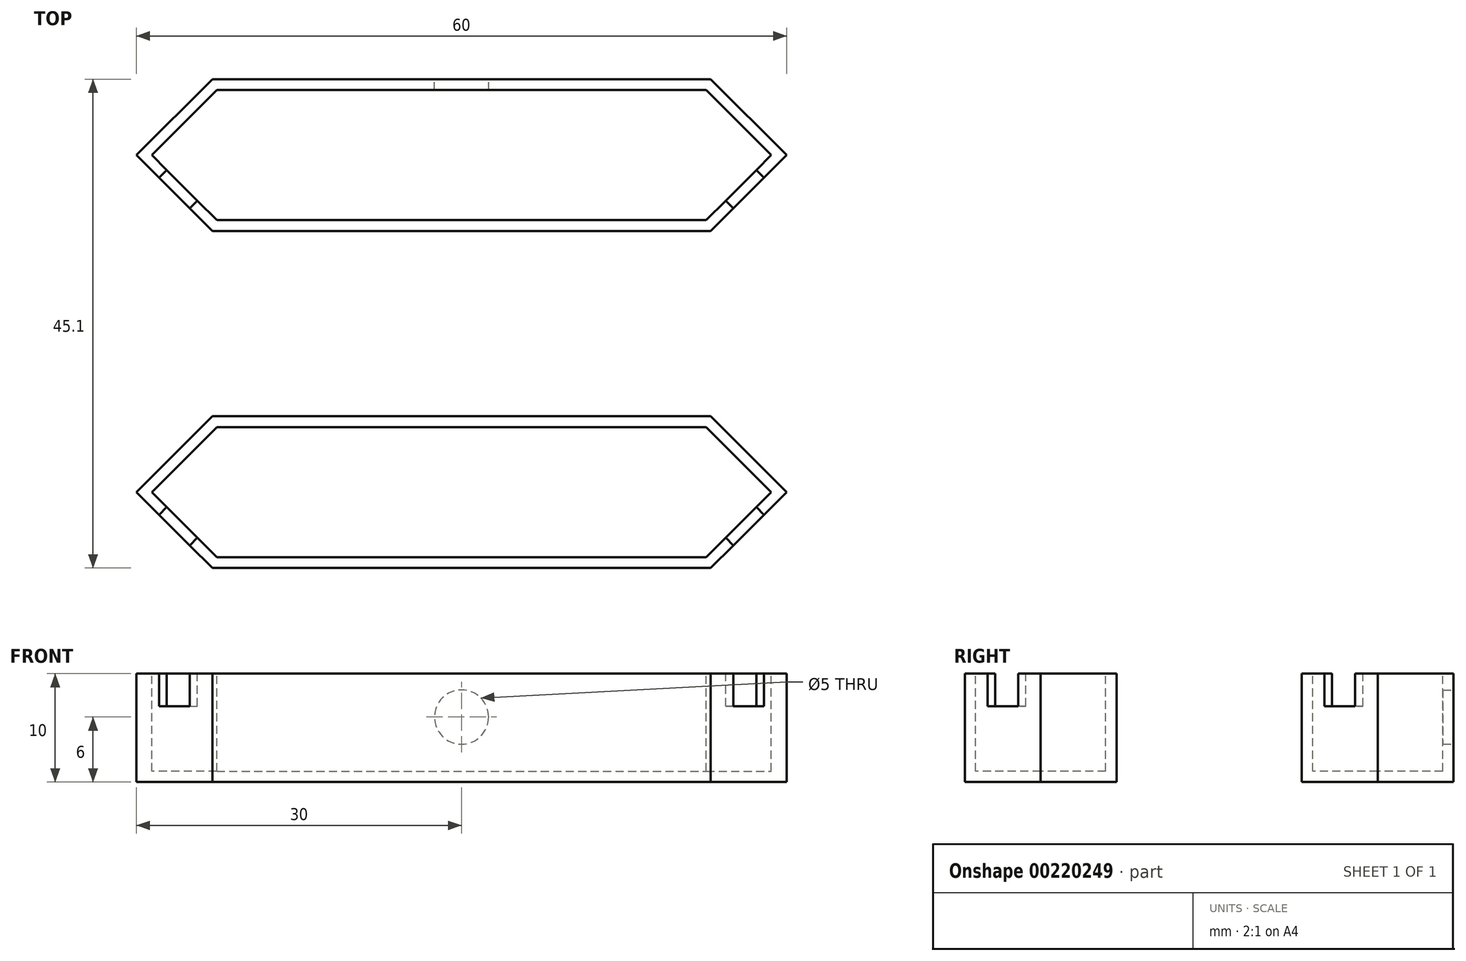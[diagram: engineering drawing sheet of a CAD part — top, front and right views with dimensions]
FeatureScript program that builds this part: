
annotation { "Feature Type Name" : "Feature", "Feature Type Description" : "" }
export const myFeature = defineFeature(function(context is Context, id is Id, definition is map)
    precondition{}
    {
        {
            assignVariable(context, id + "F0", {"name" : "breite", "anyValue" : 14});
        }
        {
            assignVariable(context, id + "F1", {"name" : "hoehe", "anyValue" : 10});
        }
        {
            assignVariable(context, id + "F2", {"name" : "wandung", "anyValue" : 1});
        }
        {
            var Q0;
            Q0=qCreatedBy(makeId("Top.planeOp"),FACE);
            var sketch = newSketch(context, id + "F3", { "sketchPlane" : qUnion([Q0])});
            skLineSegment(sketch, "E0.bottom", {"start": v(-30, 7) * mm, "end": v(30, 7) * mm});
            skLineSegment(sketch, "E0.top", {"start": v(-30, -7) * mm, "end": v(30, -7) * mm});
            skLineSegment(sketch, "E0.left", {"start": v(-30, 7) * mm, "end": v(-30, -7) * mm});
            skLineSegment(sketch, "E0.right", {"start": v(30, 7) * mm, "end": v(30, -7) * mm});
            skSolve(sketch);
        }
        {
            var Q0;
            Q0=makeQuery(id+"F3.imprint","IMPRINT",FACE,{"disambiguationData":[TD([[makeQuery(id+"F3.imprint","IMPRINT",EDGE,{"derivedFrom":sQuery(id+"F3.wireOp",EDGE,"E0.bottom")}),-1.0]])]});
            extrude(context, id + "F4", {"entities" : qUnion([Q0]), "depth" : (getVariable(context, 'hoehe')) * mm});
        }
        {
            var Q0;
            Q0=makeQuery(id+"F4.opExtrude","SWEPT_EDGE",EDGE,{"disambiguationData":[OSD([sQuery(id+"F3.wireOp",EDGE,"E0.top"),sQuery(id+"F3.wireOp",EDGE,"E0.left")])]});
            var Q1;
            Q1=makeQuery(id+"F4.opExtrude","SWEPT_EDGE",EDGE,{"disambiguationData":[OSD([sQuery(id+"F3.wireOp",EDGE,"E0.bottom"),sQuery(id+"F3.wireOp",EDGE,"E0.left")])]});
            var Q2;
            Q2=makeQuery(id+"F4.opExtrude","SWEPT_EDGE",EDGE,{"disambiguationData":[OSD([sQuery(id+"F3.wireOp",EDGE,"E0.top"),sQuery(id+"F3.wireOp",EDGE,"E0.right")])]});
            var Q3;
            Q3=makeQuery(id+"F4.opExtrude","SWEPT_EDGE",EDGE,{"disambiguationData":[OSD([sQuery(id+"F3.wireOp",EDGE,"E0.bottom"),sQuery(id+"F3.wireOp",EDGE,"E0.right")])]});
            chamfer(context, id + "F5", {"entities" : qUnion([Q0, Q1, Q2, Q3]), "width" : (getVariable(context, 'breite') / 2) * mm, "tangentPropagation" : true});
        }
        {
            var Q0;
            Q0=makeQuery(id+"F4.opExtrude","CAP_FACE",FACE,{"disambiguationData":[OSD([sQuery(id+"F3.wireOp",EDGE,"E0.bottom"),sQuery(id+"F3.wireOp",EDGE,"E0.top"),sQuery(id+"F3.wireOp",EDGE,"E0.left"),sQuery(id+"F3.wireOp",EDGE,"E0.right")])],"isStart":false});
            var sketch = newSketch(context, id + "F6", { "sketchPlane" : qUnion([Q0])});
            skLineSegment(sketch, "E1.0", {"start": v(-22.59, 6) * mm, "end": v(-28.59, 0) * mm});
            skLineSegment(sketch, "E1.1", {"start": v(28.59, 0) * mm, "end": v(22.59, 6) * mm});
            skLineSegment(sketch, "E1.2", {"start": v(22.59, -6) * mm, "end": v(28.59, 0) * mm});
            skLineSegment(sketch, "E1.3", {"start": v(-22.59, 6) * mm, "end": v(22.59, 6) * mm});
            skLineSegment(sketch, "E1.4", {"start": v(-22.59, -6) * mm, "end": v(22.59, -6) * mm});
            skLineSegment(sketch, "E1.5", {"start": v(-28.59, 0) * mm, "end": v(-22.59, -6) * mm});
            skSolve(sketch);
        }
        {
            var Q0;
            Q0=makeQuery(id+"F6.imprint","IMPRINT",FACE,{"disambiguationData":[TD([[makeQuery(id+"F6.imprint","IMPRINT",EDGE,{"derivedFrom":sQuery(id+"F6.wireOp",EDGE,"E1.0")}),1.0]])]});
            extrude(context, id + "F7", {"entities" : qUnion([Q0]), "operationType" : NewBodyOperationType.REMOVE, "oppositeDirection" : true, "depth" : (getVariable(context, 'hoehe') - 1) * mm});
        }
        {
            var Q0;
            Q0=makeQuery(id+"F4.opExtrude","CAP_FACE",FACE,{"disambiguationData":[OSD([sQuery(id+"F3.wireOp",EDGE,"E0.bottom"),sQuery(id+"F3.wireOp",EDGE,"E0.top"),sQuery(id+"F3.wireOp",EDGE,"E0.left"),sQuery(id+"F3.wireOp",EDGE,"E0.right")])],"isStart":false});
            var sketch = newSketch(context, id + "F8", { "sketchPlane" : qUnion([Q0])});
            skLineSegment(sketch, "E2", {"start": v(-27.91, -2.09) * mm, "end": v(-25.09, -4.91) * mm});
            skLineSegment(sketch, "E3", {"start": v(-25.09, -4.91) * mm, "end": v(-24.38, -4.2) * mm});
            skLineSegment(sketch, "E4", {"start": v(-24.38, -4.2) * mm, "end": v(-27.2, -1.38) * mm});
            skLineSegment(sketch, "E5", {"start": v(-27.2, -1.38) * mm, "end": v(-27.91, -2.09) * mm});
            skLineSegment(sketch, "E6", {"start": v(24.38, -4.2) * mm, "end": v(27.2, -1.38) * mm});
            skLineSegment(sketch, "E7", {"start": v(27.2, -1.38) * mm, "end": v(27.91, -2.09) * mm});
            skLineSegment(sketch, "E8", {"start": v(27.91, -2.09) * mm, "end": v(25.09, -4.91) * mm});
            skLineSegment(sketch, "E9", {"start": v(25.09, -4.91) * mm, "end": v(24.38, -4.2) * mm});
            skSolve(sketch);
        }
        {
            var Q0;
            Q0=makeQuery(id+"F8.imprint","IMPRINT",FACE,{"disambiguationData":[TD([[makeQuery(id+"F8.imprint","IMPRINT",EDGE,{"derivedFrom":sQuery(id+"F8.wireOp",EDGE,"E2")}),1.0]])]});
            var Q1;
            Q1=makeQuery(id+"F8.imprint","IMPRINT",FACE,{"disambiguationData":[TD([[makeQuery(id+"F8.imprint","IMPRINT",EDGE,{"derivedFrom":sQuery(id+"F8.wireOp",EDGE,"E6")}),-1.0]])]});
            extrude(context, id + "F9", {"entities" : qUnion([Q0, Q1]), "operationType" : NewBodyOperationType.REMOVE, "oppositeDirection" : true, "depth" : 3 * mm});
        }
        {
            var Q0;
            Q0=makeQuery(id+"F4.opExtrude","SWEPT_BODY",BODY,{"disambiguationData":[OSD([sQuery(id+"F3.wireOp",EDGE,"E0.bottom"),sQuery(id+"F3.wireOp",EDGE,"E0.top"),sQuery(id+"F3.wireOp",EDGE,"E0.left"),sQuery(id+"F3.wireOp",EDGE,"E0.right")])]});
            transform(context, id + "F10", {"entities" : qUnion([Q0]), "transformType" : TransformType.TRANSLATION_3D, "dx" : 0 * mm, "dy" : 31.1 * mm, "dz" : 0 * mm, "makeCopy" : true});
        }
        {
            var Q0;
            Q0=makeQuery(id+"F10.opPattern","COPY",FACE,{"derivedFrom":makeQuery(id+"F4.opExtrude","SWEPT_FACE",FACE,{"disambiguationData":[OSD([sQuery(id+"F3.wireOp",EDGE,"E0.bottom")])]}),"instanceName":"1"});
            var sketch = newSketch(context, id + "F11", { "sketchPlane" : qUnion([Q0])});
            skCircle(sketch, "E10", {"center": v(0, 6) * mm, "radius": 2.5 * mm});
            skSolve(sketch);
        }
        {
            var Q0;
            Q0=makeQuery(id+"F11.imprint","IMPRINT",FACE,{"disambiguationData":[TD([[makeQuery(id+"F11.imprint","IMPRINT",EDGE,{"derivedFrom":sQuery(id+"F11.wireOp",EDGE,"E10")}),1.0]])]});
            extrude(context, id + "F12", {"entities" : qUnion([Q0]), "operationType" : NewBodyOperationType.REMOVE, "oppositeDirection" : true, "depth" : (getVariable(context, 'wandung')) * mm});
        }
    });
